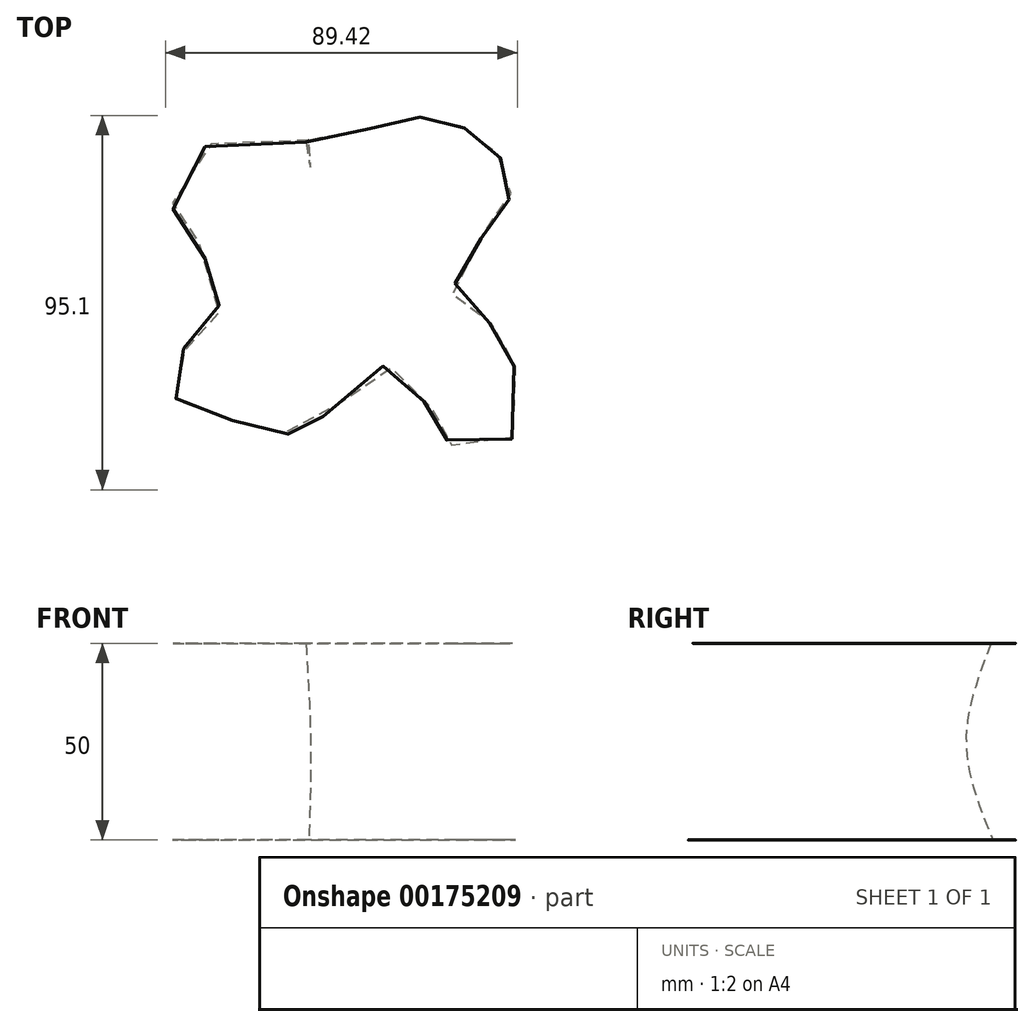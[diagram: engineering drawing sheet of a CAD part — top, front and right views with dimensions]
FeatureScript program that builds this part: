
annotation { "Feature Type Name" : "Feature", "Feature Type Description" : "" }
export const myFeature = defineFeature(function(context is Context, id is Id, definition is map)
    precondition{}
    {
        {
            var Q0;
            Q0=qCreatedBy(makeId("Top.planeOp"),FACE);
            cPlane(context, id + "F0", {"entities" : qUnion([Q0]), "cplaneType" : CPlaneType.OFFSET, "offset" : 25 * mm, "width" : 150 * mm, "height" : 150 * mm});
        }
        {
            var Q0;
            Q0=qCreatedBy(makeId("Top.planeOp"),FACE);
            cPlane(context, id + "F1", {"entities" : qUnion([Q0]), "cplaneType" : CPlaneType.OFFSET, "offset" : 25 * mm, "oppositeDirection" : true, "width" : 150 * mm, "height" : 150 * mm});
        }
        {
            var Q0;
            Q0=qCreatedBy(id+"F0.planeOp",FACE);
            var sketch = newSketch(context, id + "F2", { "sketchPlane" : qUnion([Q0])});
            skFitSpline(sketch, "E0", {"points": [v(0, 38.51) * mm, v(-29.41, 35.23) * mm, v(-33.57, 20.63) * mm, v(-32.08, 18) * mm, v(-21.08, 2.05) * mm, v(-20.71, 0) * mm, v(-27.3, -11.41) * mm, v(-31.62, -14.58) * mm, v(-34.45, -24.69) * mm, v(-26.79, -29.2) * mm, v(-15, -33.55) * mm, v(-5.08, -35.64) * mm, v(0, -35.46) * mm, v(4.1, -31.54) * mm, v(19.31, -18.48) * mm, v(25.1, -22.05) * mm, v(31.82, -30.5) * mm, v(32.56, -34.8) * mm, v(49.03, -39.91) * mm, v(53.36, -30.75) * mm, v(52.1, -13.33) * mm, v(48.37, -7.89) * mm, v(39.39, -5.24) * mm, v(39.8, 9.74) * mm, v(43.94, 13.47) * mm, v(49.2, 19.26) * mm, v(52.03, 25.06) * mm, v(51.67, 31.06) * mm, v(47.75, 36.5) * mm, v(43.46, 40.44) * mm, v(32.8, 44.78) * mm, v(29.61, 44.98) * mm, v(24.55, 43.3) * mm, v(13.68, 41.47) * mm, v(0, 38.51) * mm]});
            skSolve(sketch);
        }
        {
            var Q0;
            Q0=qCreatedBy(makeId("Top.planeOp"),FACE);
            var sketch = newSketch(context, id + "F3", { "sketchPlane" : qUnion([Q0])});
            skFitSpline(sketch, "E1", {"points": [v(0, 31.95) * mm, v(-14.76, 29.96) * mm, v(-19.07, 28.1) * mm, v(-29.6, 18.6) * mm, v(-33.18, 14.88) * mm, v(-35.27, 9.27) * mm, v(-35.48, 4.4) * mm, v(-31.22, -4.99) * mm, v(-26.55, -8.57) * mm, v(-23.76, -12.89) * mm, v(-20.98, -18.7) * mm, v(-18.2, -25.46) * mm, v(-20.29, -30.14) * mm, v(-22.54, -32) * mm, v(-25.36, -33.67) * mm, v(-27.07, -39.28) * mm, v(-22.79, -43.8) * mm, v(-16.05, -44.77) * mm, v(-12.68, -44.6) * mm, v(-3.29, -39.02) * mm, v(2.72, -36.8) * mm, v(12.63, -39.1) * mm, v(16.17, -43.05) * mm, v(22.14, -48.32) * mm, v(31.68, -49.3) * mm, v(37.12, -49.33) * mm, v(40.71, -41.67) * mm, v(40.73, -37.73) * mm, v(38.52, -29.1) * mm, v(36.85, -26.1) * mm, v(32.03, -16.34) * mm, v(32.04, -13.72) * mm, v(42.03, 0) * mm, v(43.16, 0) * mm, v(45.63, 7.95) * mm, v(45.64, 10.76) * mm, v(41.35, 14.71) * mm, v(37.62, 16.98) * mm, v(34.63, 19.8) * mm, v(28.1, 23.95) * mm, v(15.94, 27.38) * mm, v(12.96, 30.02) * mm, v(14.48, 33.94) * mm, v(15.23, 34.88) * mm, v(0, 31.95) * mm]});
            skSolve(sketch);
        }
        {
            var Q0;
            Q0=qCreatedBy(id+"F1.planeOp",FACE);
            var sketch = newSketch(context, id + "F4", { "sketchPlane" : qUnion([Q0])});
            skFitSpline(sketch, "E2", {"points": [v(0, 38.9) * mm, v(-29.53, 35.32) * mm, v(-33.74, 20.37) * mm, v(-32.25, 17.74) * mm, v(-20.36, 1.94) * mm, v(-27.74, -11.5) * mm, v(-30.94, -14.67) * mm, v(-34.75, -24.95) * mm, v(-26.72, -28.93) * mm, v(-14.76, -33.87) * mm, v(-5.03, -35.23) * mm, v(4.54, -31.54) * mm, v(19.6, -18.33) * mm, v(25.2, -22.67) * mm, v(32.46, -30.2) * mm, v(32.61, -35.45) * mm, v(48.88, -40.04) * mm, v(53.62, -30.7) * mm, v(52.4, -13.46) * mm, v(48.32, -8) * mm, v(38.97, -5.7) * mm, v(40, 9.83) * mm, v(49.03, 18.58) * mm, v(52.06, 25.12) * mm, v(51.73, 31.49) * mm, v(47.63, 36.57) * mm, v(43.16, 40.53) * mm, v(32.7, 44.9) * mm, v(29.7, 45.1) * mm, v(24.64, 43.07) * mm, v(13.4, 41.45) * mm, v(0, 38.9) * mm]});
            skSolve(sketch);
        }
        {
            var Q0;
            Q0=makeQuery(id+"F2.imprint","IMPRINT",FACE,{"disambiguationData":[TD([[makeQuery(id+"F2.imprint","IMPRINT",EDGE,{"derivedFrom":sQuery(id+"F2.wireOp",EDGE,"E0")}),1.0]])]});
            var Q1;
            Q1=makeQuery(id+"F3.imprint","IMPRINT",FACE,{"disambiguationData":[TD([[makeQuery(id+"F3.imprint","IMPRINT",EDGE,{"derivedFrom":sQuery(id+"F3.wireOp",EDGE,"E1")}),1.0]])]});
            var Q2;
            Q2=makeQuery(id+"F4.imprint","IMPRINT",FACE,{"disambiguationData":[TD([[makeQuery(id+"F4.imprint","IMPRINT",EDGE,{"derivedFrom":sQuery(id+"F4.wireOp",EDGE,"E2")}),1.0]])]});
            loft(context, id + "F5", {"sheetProfilesArray" : [{ "sheetProfileEntities" : qUnion([Q0]) }, { "sheetProfileEntities" : qUnion([Q1]) }, { "sheetProfileEntities" : qUnion([Q2]) }]});
        }
    });
